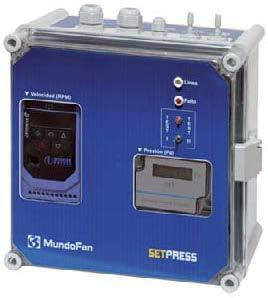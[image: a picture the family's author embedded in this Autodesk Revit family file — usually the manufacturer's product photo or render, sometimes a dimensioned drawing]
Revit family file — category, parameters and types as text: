
# Revit family: SETPRESS-75_VE10813
name_source: partatom
category: Aparatos eléctricos
revit_build: Autodesk Revit 2016 (Build: 20150220_1215(x64)
units: mm (PartAtom-declared; Revit-internal decimal feet)

## family parameters
Compartido = No
Corte con vacíos al cargar = No
Cota de conector redondo = Diámetro de uso
Mantener orientación de anotación = No
Número OmniClass = 23.80.00.00
Punto de cálculo de habitación = No
Se basa en plano de trabajo = No
Siempre vertical = Sí
Tipo de pieza = Caja de conexiones
Título OmniClass = Electric Power and Lighting

## types (1)
- SETPRESS
    Alimentación = 400Vac trifásico
    Corriente = 18 A
    Costo = 0 $
    Código de montaje = VE10813
    Descripción = CONTROL EFICIENCIA ENERGETICA PARA VENTILADORES
    Dimensiones máx. = 270x300x170 mm
    Fabricante = SALVADOR ESCODA
    Imagen de tipo = setpress.jpg
    Leds = linea / fallo
    Modelo = SETPRESS 7,5 kW
    Normativas = UNE-EN 12101-6
    Potencia = 7,5 kW
    Regulación = Mediante sonda analógica de presión
    Salida = 400Vac trifásico
    URL = www.salvadorescoda.com
    Visualización = frecuencia (Hz) y presión (Pa)
